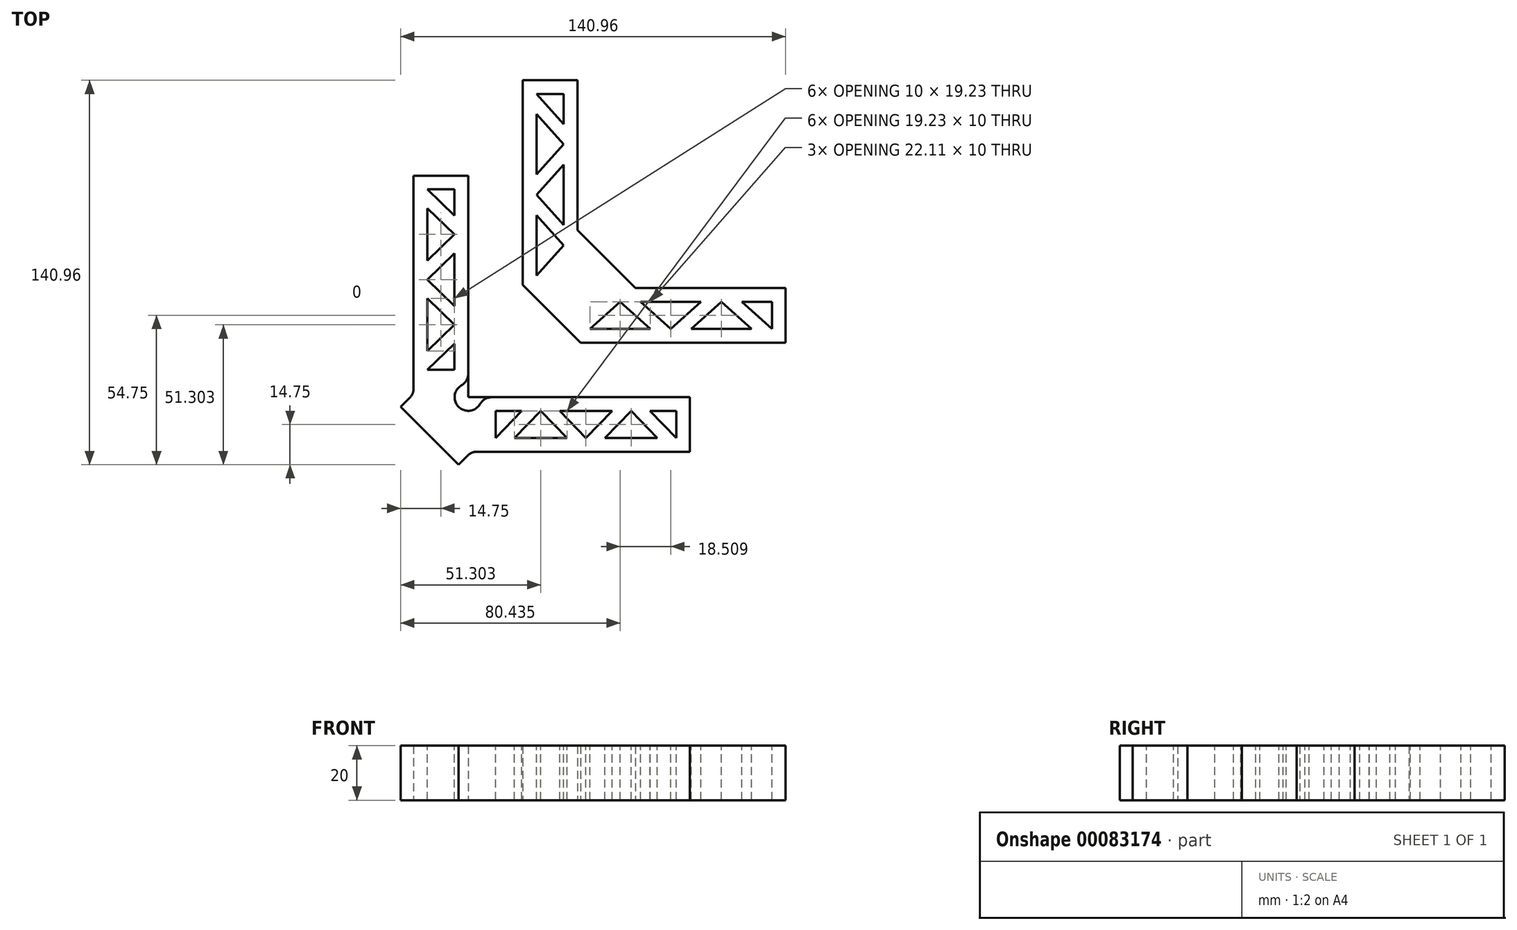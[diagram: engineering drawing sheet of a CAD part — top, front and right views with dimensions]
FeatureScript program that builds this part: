
annotation { "Feature Type Name" : "Feature", "Feature Type Description" : "" }
export const myFeature = defineFeature(function(context is Context, id is Id, definition is map)
    precondition{}
    {
        {
            assignVariable(context, id + "F0", {"name" : "Brace_Height", "anyValue" : 20});
        }
        {
            var Q0;
            Q0=qCreatedBy(makeId("Top.planeOp"),FACE);
            var sketch = newSketch(context, id + "F1", { "sketchPlane" : qUnion([Q0])});
            skLineSegment(sketch, "E0", {"start": v(0, 8.66) * mm, "end": v(0, 81.21) * mm});
            skLineSegment(sketch, "E1", {"start": v(0, 81.21) * mm, "end": v(-20, 81.21) * mm});
            skLineSegment(sketch, "E2", {"start": v(-20, 81.21) * mm, "end": v(-20, 3.28) * mm});
            skLineSegment(sketch, "E3", {"start": v(3.28, -20) * mm, "end": v(81.21, -20) * mm});
            skLineSegment(sketch, "E4", {"start": v(81.21, -20) * mm, "end": v(81.21, 0) * mm});
            skLineSegment(sketch, "E5", {"start": v(81.21, 0) * mm, "end": v(8.66, 0) * mm});
            skArc(sketch, "E6", {"start": v(-2.5, 4.33) * mm, "mid": v(-3.54, -3.54) * mm, "end": v(4.33, -2.5) * mm});
            skLineSegment(sketch, "E7", {"start": v(-21.46, -0.25) * mm, "end": v(-24.75, -3.54) * mm});
            skLineSegment(sketch, "E8", {"start": v(-24.75, -3.54) * mm, "end": v(-3.54, -24.75) * mm});
            skLineSegment(sketch, "E9", {"start": v(-3.54, -24.75) * mm, "end": v(-0.25, -21.46) * mm});
            skLineSegment(sketch, "E10", {"start": v(-14.14, -14.14) * mm, "end": v(0, 0) * mm, "construction": true});
            skPoint(sketch, "E11.visualSharp", {"position": v(5, 0) * mm});
            skArc(sketch, "E11.filletArc", {"start": v(8.66, 0) * mm, "mid": v(6.16, -0.67) * mm, "end": v(4.33, -2.5) * mm});
            skPoint(sketch, "E12.visualSharp", {"position": v(0, 5) * mm});
            skArc(sketch, "E12.filletArc", {"start": v(-2.5, 4.33) * mm, "mid": v(-0.67, 6.16) * mm, "end": v(0, 8.66) * mm});
            skPoint(sketch, "E13.visualSharp", {"position": v(-20, 1.21) * mm});
            skArc(sketch, "E13.filletArc", {"start": v(-21.46, -0.25) * mm, "mid": v(-20.38, 1.37) * mm, "end": v(-20, 3.28) * mm});
            skPoint(sketch, "E14.visualSharp", {"position": v(1.21, -20) * mm});
            skArc(sketch, "E14.filletArc", {"start": v(3.28, -20) * mm, "mid": v(1.37, -20.38) * mm, "end": v(-0.25, -21.46) * mm});
            skLineSegment(sketch, "E15", {"start": v(20, 116.21) * mm, "end": v(20, 41.21) * mm});
            skLineSegment(sketch, "E16", {"start": v(41.21, 20) * mm, "end": v(116.21, 20) * mm});
            skLineSegment(sketch, "E17", {"start": v(116.21, 20) * mm, "end": v(116.21, 40) * mm});
            skLineSegment(sketch, "E18", {"start": v(116.21, 40) * mm, "end": v(61.21, 40) * mm});
            skLineSegment(sketch, "E19", {"start": v(40, 61.21) * mm, "end": v(40, 116.21) * mm});
            skLineSegment(sketch, "E20", {"start": v(40, 116.21) * mm, "end": v(20, 116.21) * mm});
            skLineSegment(sketch, "E21", {"start": v(40, 61.21) * mm, "end": v(61.21, 40) * mm});
            skPoint(sketch, "E22.visualSharp", {"position": v(20, 20) * mm});
            skLineSegment(sketch, "E23", {"start": v(20, 41.21) * mm, "end": v(41.21, 20) * mm});
            skSolve(sketch);
        }
        {
            var Q0;
            Q0=qCreatedBy(makeId("Top.planeOp"),FACE);
            var sketch = newSketch(context, id + "F2", { "sketchPlane" : qUnion([Q0])});
            skLineSegment(sketch, "E24.0.0", {"start": v(40, 116.21) * mm, "end": v(20, 116.21) * mm});
            skLineSegment(sketch, "E24.0.1", {"start": v(20, 116.21) * mm, "end": v(20, 41.21) * mm});
            skLineSegment(sketch, "E24.0.2", {"start": v(20, 41.21) * mm, "end": v(41.21, 20) * mm});
            skLineSegment(sketch, "E24.0.3", {"start": v(41.21, 20) * mm, "end": v(116.21, 20) * mm});
            skLineSegment(sketch, "E24.0.4", {"start": v(116.21, 20) * mm, "end": v(116.21, 40) * mm});
            skLineSegment(sketch, "E24.0.5", {"start": v(116.21, 40) * mm, "end": v(61.21, 40) * mm});
            skLineSegment(sketch, "E24.0.6", {"start": v(61.21, 40) * mm, "end": v(40, 61.21) * mm});
            skLineSegment(sketch, "E24.0.7", {"start": v(40, 61.21) * mm, "end": v(40, 116.21) * mm});
            skLineSegment(sketch, "E25.0.1", {"start": v(0, 0) * mm, "end": v(0, 81.21) * mm});
            skLineSegment(sketch, "E25.0.2", {"start": v(0, 81.21) * mm, "end": v(-20, 81.21) * mm});
            skLineSegment(sketch, "E25.0.3", {"start": v(-20, 81.21) * mm, "end": v(-20, 3.28) * mm});
            skArc(sketch, "E25.0.4", {"start": v(-20, 3.28) * mm, "mid": v(-20.38, 1.37) * mm, "end": v(-21.46, -0.25) * mm});
            skLineSegment(sketch, "E25.0.5", {"start": v(-21.46, -0.25) * mm, "end": v(-24.75, -3.54) * mm});
            skLineSegment(sketch, "E25.0.6", {"start": v(-24.75, -3.54) * mm, "end": v(-3.54, -24.75) * mm});
            skLineSegment(sketch, "E25.0.7", {"start": v(-3.54, -24.75) * mm, "end": v(-0.25, -21.46) * mm});
            skArc(sketch, "E25.0.8", {"start": v(-0.25, -21.46) * mm, "mid": v(1.37, -20.38) * mm, "end": v(3.28, -20) * mm});
            skLineSegment(sketch, "E25.0.9", {"start": v(3.28, -20) * mm, "end": v(81.21, -20) * mm});
            skLineSegment(sketch, "E25.0.10", {"start": v(81.21, -20) * mm, "end": v(81.21, 0) * mm});
            skLineSegment(sketch, "E25.0.11", {"start": v(81.21, 0) * mm, "end": v(0, 0) * mm});
            skSolve(sketch);
        }
        {
            var Q0;
            Q0 = qSketchRegion(id + "F2", true);
            extrude(context, id + "F3", {"entities" : qUnion([Q0]), "depth" : (getVariable(context, 'Brace_Height')) * mm});
        }
        {
            var Q0;
            Q0=makeQuery(id+"F1.imprint","IMPRINT",FACE,{"disambiguationData":[TD([[makeQuery(id+"F1.imprint","IMPRINT",EDGE,{"derivedFrom":sQuery(id+"F1.wireOp",EDGE,"E0")}),1.0]])]});
            extrude(context, id + "F4", {"entities" : qUnion([Q0]), "depth" : (getVariable(context, 'Brace_Height')) * mm});
        }
        {
            var Q0;
            Q0=qCreatedBy(makeId("Top.planeOp"),FACE);
            var sketch = newSketch(context, id + "F5", { "sketchPlane" : qUnion([Q0])});
            skLineSegment(sketch, "E26.0.0", {"start": v(81.21, 0) * mm, "end": v(0, 0) * mm, "construction": true});
            skLineSegment(sketch, "E26.0.1", {"start": v(0, 0) * mm, "end": v(0, 81.21) * mm, "construction": true});
            skLineSegment(sketch, "E26.0.2", {"start": v(0, 81.21) * mm, "end": v(-20, 81.21) * mm, "construction": true});
            skLineSegment(sketch, "E26.0.3", {"start": v(-20, 81.21) * mm, "end": v(-20, 3.28) * mm, "construction": true});
            skArc(sketch, "E26.0.4", {"start": v(-20, 3.28) * mm, "mid": v(-20.38, 1.37) * mm, "end": v(-21.46, -0.25) * mm, "construction": true});
            skLineSegment(sketch, "E26.0.5", {"start": v(-21.46, -0.25) * mm, "end": v(-24.75, -3.54) * mm, "construction": true});
            skLineSegment(sketch, "E26.0.6", {"start": v(-24.75, -3.54) * mm, "end": v(-3.54, -24.75) * mm, "construction": true});
            skLineSegment(sketch, "E26.0.7", {"start": v(-3.54, -24.75) * mm, "end": v(-0.25, -21.46) * mm, "construction": true});
            skArc(sketch, "E26.0.8", {"start": v(-0.25, -21.46) * mm, "mid": v(1.37, -20.38) * mm, "end": v(3.28, -20) * mm, "construction": true});
            skLineSegment(sketch, "E26.0.9", {"start": v(3.28, -20) * mm, "end": v(81.21, -20) * mm, "construction": true});
            skLineSegment(sketch, "E26.0.10", {"start": v(81.21, -20) * mm, "end": v(81.21, 0) * mm, "construction": true});
            skLineSegment(sketch, "E27.0.0", {"start": v(40, 61.21) * mm, "end": v(40, 116.21) * mm, "construction": true});
            skLineSegment(sketch, "E27.0.1", {"start": v(40, 116.21) * mm, "end": v(20, 116.21) * mm, "construction": true});
            skLineSegment(sketch, "E27.0.2", {"start": v(20, 116.21) * mm, "end": v(20, 41.21) * mm, "construction": true});
            skLineSegment(sketch, "E27.0.3", {"start": v(20, 41.21) * mm, "end": v(41.21, 20) * mm, "construction": true});
            skLineSegment(sketch, "E27.0.4", {"start": v(41.21, 20) * mm, "end": v(116.21, 20) * mm, "construction": true});
            skLineSegment(sketch, "E27.0.5", {"start": v(116.21, 20) * mm, "end": v(116.21, 40) * mm, "construction": true});
            skLineSegment(sketch, "E27.0.6", {"start": v(116.21, 40) * mm, "end": v(61.21, 40) * mm, "construction": true});
            skLineSegment(sketch, "E27.0.7", {"start": v(61.21, 40) * mm, "end": v(40, 61.21) * mm, "construction": true});
            skLineSegment(sketch, "E28", {"start": v(-5, 10) * mm, "end": v(-15, 10) * mm});
            skLineSegment(sketch, "E29", {"start": v(-15, 10) * mm, "end": v(-5, 19.62) * mm});
            skLineSegment(sketch, "E30", {"start": v(-5, 19.62) * mm, "end": v(-5, 10) * mm});
            skLineSegment(sketch, "E31", {"start": v(-15, 16.94) * mm, "end": v(-5, 26.55) * mm});
            skLineSegment(sketch, "E32", {"start": v(-5, 26.55) * mm, "end": v(-15, 36.17) * mm});
            skLineSegment(sketch, "E33", {"start": v(-15, 36.17) * mm, "end": v(-15, 16.94) * mm});
            skLineSegment(sketch, "E34", {"start": v(-15, 43.1) * mm, "end": v(-5, 33.5) * mm});
            skLineSegment(sketch, "E35", {"start": v(-5, 33.5) * mm, "end": v(-5, 52.72) * mm});
            skLineSegment(sketch, "E36", {"start": v(-5, 52.72) * mm, "end": v(-15, 43.1) * mm});
            skLineSegment(sketch, "E37", {"start": v(-15, 50.04) * mm, "end": v(-5, 59.66) * mm});
            skLineSegment(sketch, "E38", {"start": v(-5, 59.66) * mm, "end": v(-15, 69.28) * mm});
            skLineSegment(sketch, "E39", {"start": v(-15, 69.28) * mm, "end": v(-15, 50.04) * mm});
            skLineSegment(sketch, "E40", {"start": v(-15, 76.21) * mm, "end": v(-5, 66.6) * mm});
            skLineSegment(sketch, "E41", {"start": v(-5, 66.6) * mm, "end": v(-5, 76.21) * mm});
            skLineSegment(sketch, "E42", {"start": v(-5, 76.21) * mm, "end": v(-15, 76.21) * mm});
            skLineSegment(sketch, "E43", {"start": v(0, 0) * mm, "end": v(30.6, 30.6) * mm, "construction": true});
            skLineSegment(sketch, "E44.MirrorCS", {"start": v(33.5, -5) * mm, "end": v(52.72, -5) * mm});
            skLineSegment(sketch, "E45.MirrorCS", {"start": v(76.21, -5) * mm, "end": v(76.21, -15) * mm});
            skLineSegment(sketch, "E46.MirrorCS", {"start": v(43.1, -15) * mm, "end": v(33.5, -5) * mm});
            skLineSegment(sketch, "E47.MirrorCS", {"start": v(26.55, -5) * mm, "end": v(36.17, -15) * mm});
            skLineSegment(sketch, "E48.MirrorCS", {"start": v(10, -15) * mm, "end": v(19.62, -5) * mm});
            skLineSegment(sketch, "E49.MirrorCS", {"start": v(50.04, -15) * mm, "end": v(59.66, -5) * mm});
            skLineSegment(sketch, "E50.MirrorCS", {"start": v(52.72, -5) * mm, "end": v(43.1, -15) * mm});
            skLineSegment(sketch, "E51.MirrorCS", {"start": v(36.17, -15) * mm, "end": v(16.94, -15) * mm});
            skLineSegment(sketch, "E52.MirrorCS", {"start": v(69.28, -15) * mm, "end": v(50.04, -15) * mm});
            skLineSegment(sketch, "E53.MirrorCS", {"start": v(59.66, -5) * mm, "end": v(69.28, -15) * mm});
            skLineSegment(sketch, "E54.MirrorCS", {"start": v(66.6, -5) * mm, "end": v(76.21, -5) * mm});
            skLineSegment(sketch, "E55.MirrorCS", {"start": v(76.21, -15) * mm, "end": v(66.6, -5) * mm});
            skLineSegment(sketch, "E56.MirrorCS", {"start": v(16.94, -15) * mm, "end": v(26.55, -5) * mm});
            skLineSegment(sketch, "E57.MirrorCS", {"start": v(19.62, -5) * mm, "end": v(10, -5) * mm});
            skLineSegment(sketch, "E58.MirrorCS", {"start": v(10, -5) * mm, "end": v(10, -15) * mm});
            skLineSegment(sketch, "E59", {"start": v(25, 44.63) * mm, "end": v(35, 55.69) * mm});
            skLineSegment(sketch, "E60", {"start": v(35, 55.69) * mm, "end": v(25, 66.74) * mm});
            skLineSegment(sketch, "E61", {"start": v(25, 66.74) * mm, "end": v(25, 44.63) * mm});
            skLineSegment(sketch, "E62", {"start": v(25, 74.2) * mm, "end": v(35, 63.14) * mm});
            skLineSegment(sketch, "E63", {"start": v(35, 63.14) * mm, "end": v(35, 85.25) * mm});
            skLineSegment(sketch, "E64", {"start": v(35, 85.25) * mm, "end": v(25, 74.2) * mm});
            skLineSegment(sketch, "E65", {"start": v(25, 81.65) * mm, "end": v(35, 92.7) * mm});
            skLineSegment(sketch, "E66", {"start": v(35, 92.7) * mm, "end": v(25, 103.76) * mm});
            skLineSegment(sketch, "E67", {"start": v(25, 103.76) * mm, "end": v(25, 81.65) * mm});
            skLineSegment(sketch, "E68", {"start": v(25, 111.21) * mm, "end": v(35, 111.21) * mm});
            skLineSegment(sketch, "E69", {"start": v(35, 111.21) * mm, "end": v(35, 100.16) * mm});
            skLineSegment(sketch, "E70", {"start": v(35, 100.16) * mm, "end": v(25, 111.21) * mm});
            skLineSegment(sketch, "E71.MirrorCS", {"start": v(74.2, 25) * mm, "end": v(63.14, 35) * mm});
            skLineSegment(sketch, "E72.MirrorCS", {"start": v(81.65, 25) * mm, "end": v(92.7, 35) * mm});
            skLineSegment(sketch, "E73.MirrorCS", {"start": v(111.21, 35) * mm, "end": v(100.16, 35) * mm});
            skLineSegment(sketch, "E74.MirrorCS", {"start": v(85.25, 35) * mm, "end": v(74.2, 25) * mm});
            skLineSegment(sketch, "E75.MirrorCS", {"start": v(100.16, 35) * mm, "end": v(111.21, 25) * mm});
            skLineSegment(sketch, "E76.MirrorCS", {"start": v(66.74, 25) * mm, "end": v(44.63, 25) * mm});
            skLineSegment(sketch, "E77.MirrorCS", {"start": v(92.7, 35) * mm, "end": v(103.76, 25) * mm});
            skLineSegment(sketch, "E78.MirrorCS", {"start": v(63.14, 35) * mm, "end": v(85.25, 35) * mm});
            skLineSegment(sketch, "E79.MirrorCS", {"start": v(111.21, 25) * mm, "end": v(111.21, 35) * mm});
            skLineSegment(sketch, "E80.MirrorCS", {"start": v(55.69, 35) * mm, "end": v(66.74, 25) * mm});
            skLineSegment(sketch, "E81.MirrorCS", {"start": v(103.76, 25) * mm, "end": v(81.65, 25) * mm});
            skLineSegment(sketch, "E82.MirrorCS", {"start": v(44.63, 25) * mm, "end": v(55.69, 35) * mm});
            skSolve(sketch);
        }
        {
            var Q0;
            Q0 = qSketchRegion(id + "F5", true);
            extrude(context, id + "F6", {"entities" : qUnion([Q0]), "operationType" : NewBodyOperationType.REMOVE, "endBound" : BoundingType.SYMMETRIC, "oppositeDirection" : true, "depth" : (getVariable(context, 'Brace_Height') * 2) * mm});
        }
    });
